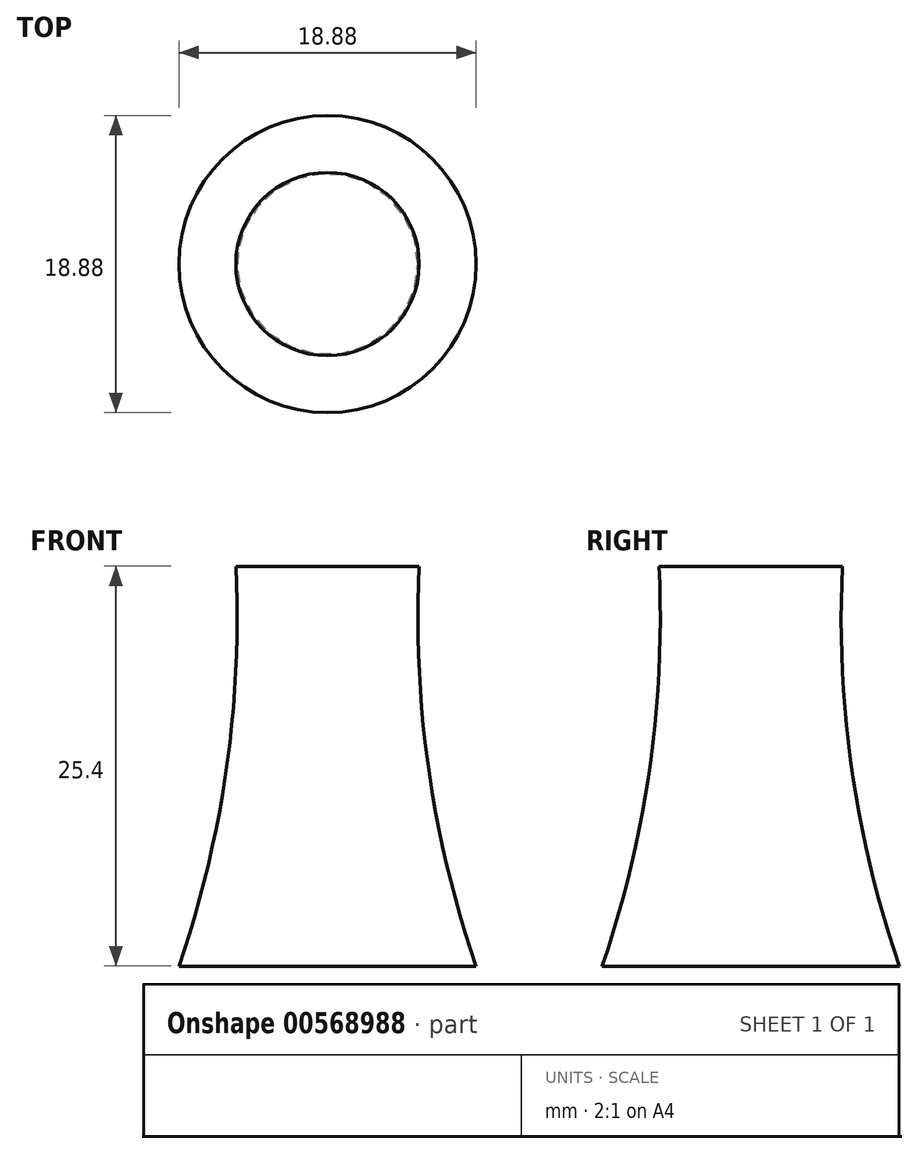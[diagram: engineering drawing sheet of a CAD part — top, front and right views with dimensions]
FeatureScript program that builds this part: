
annotation { "Feature Type Name" : "Feature", "Feature Type Description" : "" }
export const myFeature = defineFeature(function(context is Context, id is Id, definition is map)
    precondition{}
    {
        {
            var Q0;
            Q0=qCreatedBy(makeId("Front.planeOp"),FACE);
            var sketch = newSketch(context, id + "F0", { "sketchPlane" : qUnion([Q0])});
            skLineSegment(sketch, "E0", {"start": v(-5.82, 17.3) * mm, "end": v(5.82, 17.3) * mm});
            skLineSegment(sketch, "E1", {"start": v(-9.44, -8.1) * mm, "end": v(9.44, -8.1) * mm});
            skArc(sketch, "E2", {"start": v(-9.44, -8.1) * mm, "mid": v(-6.46, 4.44) * mm, "end": v(-5.82, 17.3) * mm});
            skArc(sketch, "E3", {"start": v(5.82, 17.3) * mm, "mid": v(6.42, 4.43) * mm, "end": v(9.44, -8.1) * mm});
            skLineSegment(sketch, "E4", {"start": v(0, 17.3) * mm, "end": v(0, -8.1) * mm});
            skSolve(sketch);
        }
        {
            var Q0;
            {var subQ0=sQuery(id+"F0.wireOp",EDGE,"E3");Q0=makeQuery(id+"F0.imprint","IMPRINT",FACE,{"disambiguationData":[TD([[makeQuery(id+"F0.imprint","IMPRINT",EDGE,{"derivedFrom":subQ0}),-1.0]])]});}
            var Q1;
            Q1=sQuery(id+"F0.wireOp",EDGE,"E4");
            revolve(context, id + "F1", {"entities" : qUnion([Q0]), "axis" : qUnion([Q1]), "revolveType" : RevolveType.FULL});
        }
    });
